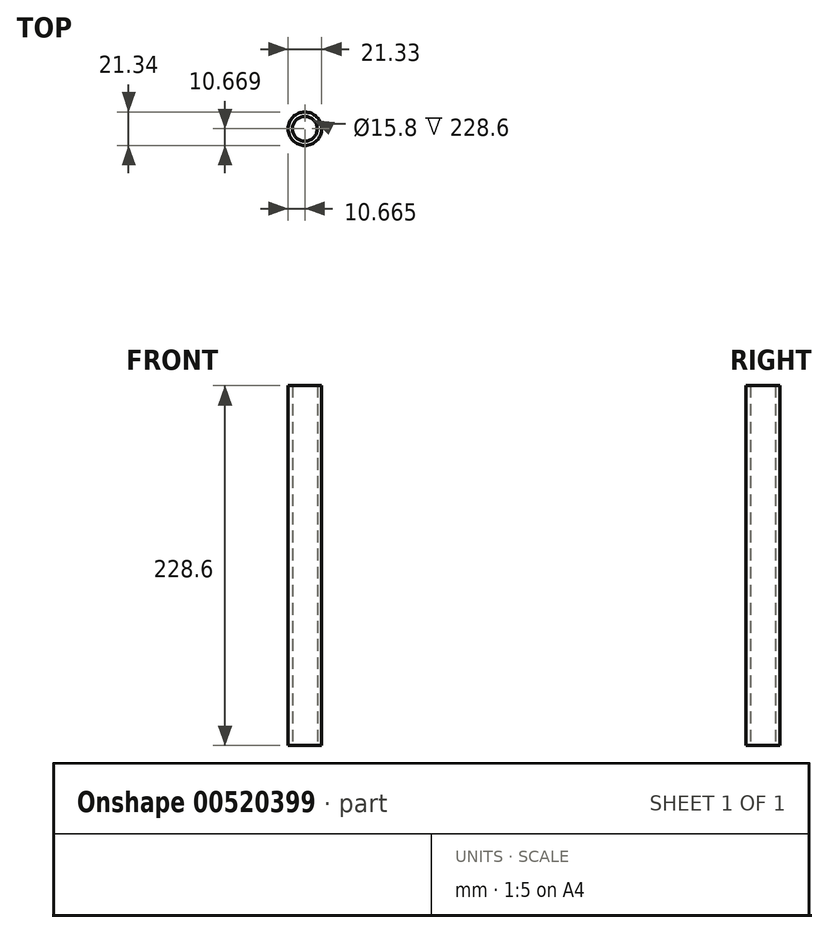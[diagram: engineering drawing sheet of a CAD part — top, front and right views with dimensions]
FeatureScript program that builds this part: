
annotation { "Feature Type Name" : "Feature", "Feature Type Description" : "" }
export const myFeature = defineFeature(function(context is Context, id is Id, definition is map)
    precondition{}
    {
        {
            var Q0;
            Q0=qCreatedBy(makeId("Top.planeOp"),FACE);
            var sketch = newSketch(context, id + "F0", { "sketchPlane" : qUnion([Q0])});
            skCircle(sketch, "E0", {"center": v(-57.88, -11.98) * mm, "radius": 10.67 * mm});
            skCircle(sketch, "E1", {"center": v(-57.88, -11.98) * mm, "radius": 7.9 * mm});
            skSolve(sketch);
        }
        {
            var Q0;
            Q0=makeQuery(id+"F0.imprint","IMPRINT",FACE,{"disambiguationData":[TD([[makeQuery(id+"F0.imprint","IMPRINT",EDGE,{"derivedFrom":sQuery(id+"F0.wireOp",EDGE,"E0")}),1.0]])]});
            extrude(context, id + "F1", {"entities" : qUnion([Q0]), "depth" : 228.6 * mm, "offsetDistance" : 25.4 * mm});
        }
    });
